# Revit family: Magnuson-Ginlet-Stools+
name_source: partatom
category: Furniture
units: mm (PartAtom-declared; Revit-internal decimal feet)

## family parameters
Always vertical = Yes
Cut with Voids When Loaded = No
OmniClass Number = 23.40.20.00
OmniClass Title = General Furniture and Specialties
Room Calculation Point = No
Shared = No
Work Plane-Based = No

## types (2) — shared parameters
Assembly Code = E2020200
Default Elevation = 0"
Depth = 15 3/8"
Glides Finish = MAG - plastic black
Keynote = 12500
Leg Finish = MAG - Textured painted steel
Low Emitting Finish = Yes
Low Emitting Material = Yes
Manufacturer = Magnuson Group
Product Documentation Link = https://magnusongroup.com
Revit Model Built By = https://servex-us.com
Salvage or Reuse = Yes
Seat Finish = MAG - plastic black
Type Comments = Stools
URL = https://magnusongroup.com
Width = 19 5/16"
zero-valued in all types: Percentage of Recycled Content

## per-type parameters (varying)
| type | B | Description | FR Dia | FR height | Height | K |
| GINLET-K | No | Counter height stool with polyurethane swivel seat, painted frame and chrome foot rest. Seat height is 24”. | 13 1/4" | 7 1/2" | 25 9/16" | Yes |
| GINLET-B | Yes | Bar height stool with polyurethane swivel seat, painted frame and chrome foot rest. Seat height is 31 5/8”. | 12 1/2" | 11" | 31 5/8" | No |

note: column(s) folded — value = type name in every type: Model

## geometry (parser evidence)
native form markers: Sweep x6
no freeform markers — native parametric forms only
